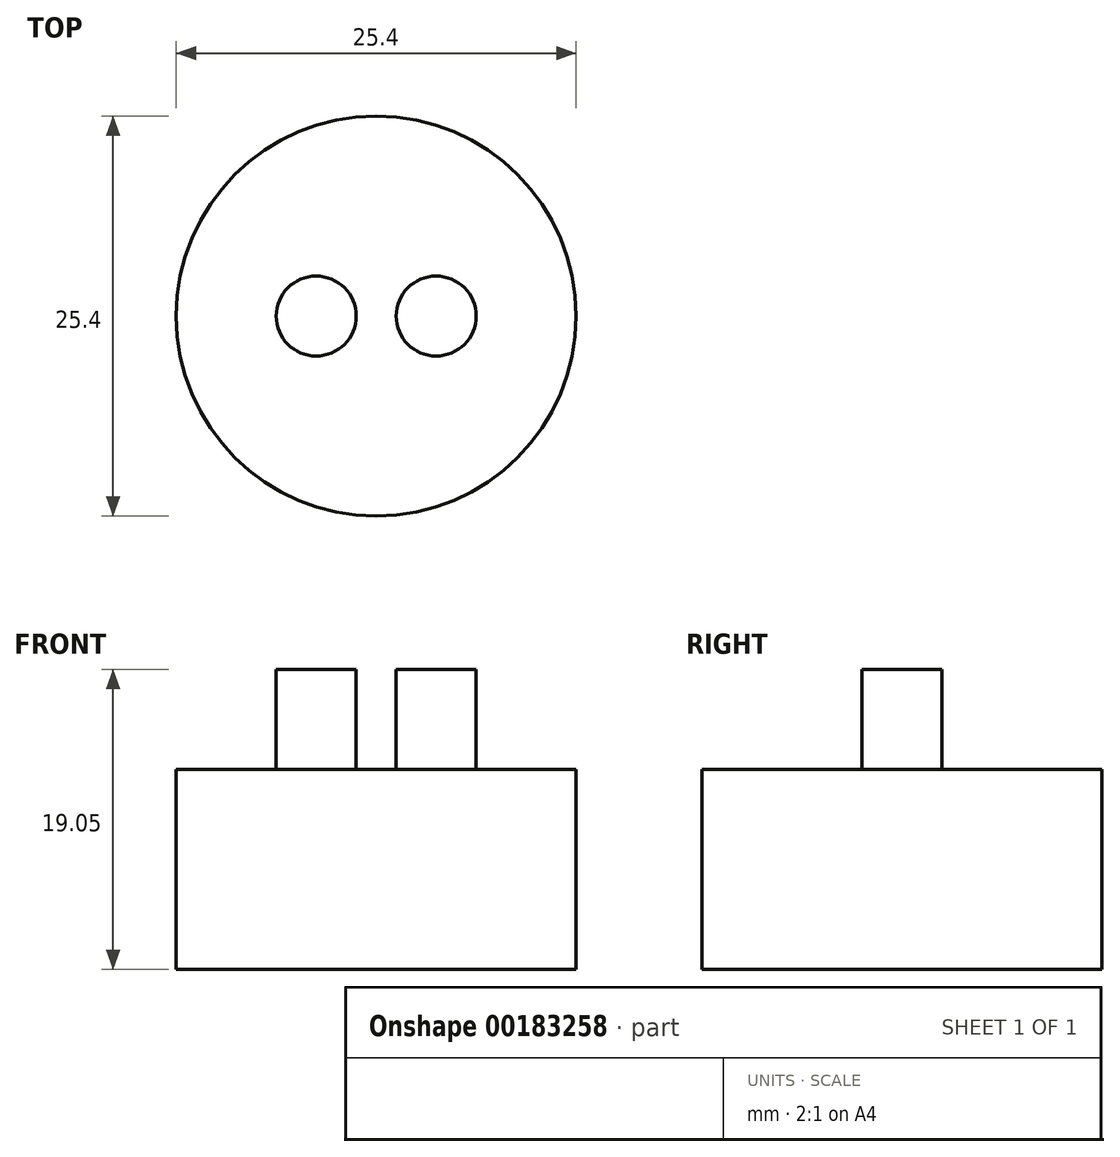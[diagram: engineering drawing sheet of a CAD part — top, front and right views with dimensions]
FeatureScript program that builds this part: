
annotation { "Feature Type Name" : "Feature", "Feature Type Description" : "" }
export const myFeature = defineFeature(function(context is Context, id is Id, definition is map)
    precondition{}
    {
        {
            var Q0;
            Q0=qCreatedBy(makeId("Top.planeOp"),FACE);
            var sketch = newSketch(context, id + "F0", { "sketchPlane" : qUnion([Q0])});
            skCircle(sketch, "E0", {"center": v(0, 0) * mm, "radius": 12.7 * mm});
            skSolve(sketch);
        }
        {
            var Q0;
            Q0=makeQuery(id+"F0.imprint","IMPRINT",FACE,{"disambiguationData":[TD([[makeQuery(id+"F0.imprint","IMPRINT",EDGE,{"derivedFrom":sQuery(id+"F0.wireOp",EDGE,"E0")}),1.0]])]});
            extrude(context, id + "F1", {"entities" : qUnion([Q0]), "depth" : 12.7 * mm});
        }
        {
            var Q0;
            Q0=makeQuery(id+"F1.opExtrude","CAP_FACE",FACE,{"disambiguationData":[OSD([sQuery(id+"F0.wireOp",EDGE,"E0")])],"isStart":false});
            var sketch = newSketch(context, id + "F2", { "sketchPlane" : qUnion([Q0])});
            skCircle(sketch, "E1", {"center": v(-3.81, 0) * mm, "radius": 2.54 * mm});
            skCircle(sketch, "E2", {"center": v(3.81, 0) * mm, "radius": 2.54 * mm});
            skSolve(sketch);
        }
        {
            var Q0;
            Q0=makeQuery(id+"F2.imprint","IMPRINT",FACE,{"disambiguationData":[TD([[makeQuery(id+"F2.imprint","IMPRINT",EDGE,{"derivedFrom":sQuery(id+"F2.wireOp",EDGE,"E1")}),1.0]])]});
            var Q1;
            Q1=makeQuery(id+"F2.imprint","IMPRINT",FACE,{"disambiguationData":[TD([[makeQuery(id+"F2.imprint","IMPRINT",EDGE,{"derivedFrom":sQuery(id+"F2.wireOp",EDGE,"E2")}),1.0]])]});
            extrude(context, id + "F3", {"entities" : qUnion([Q0, Q1]), "operationType" : NewBodyOperationType.ADD, "depth" : 6.35 * mm});
        }
    });
